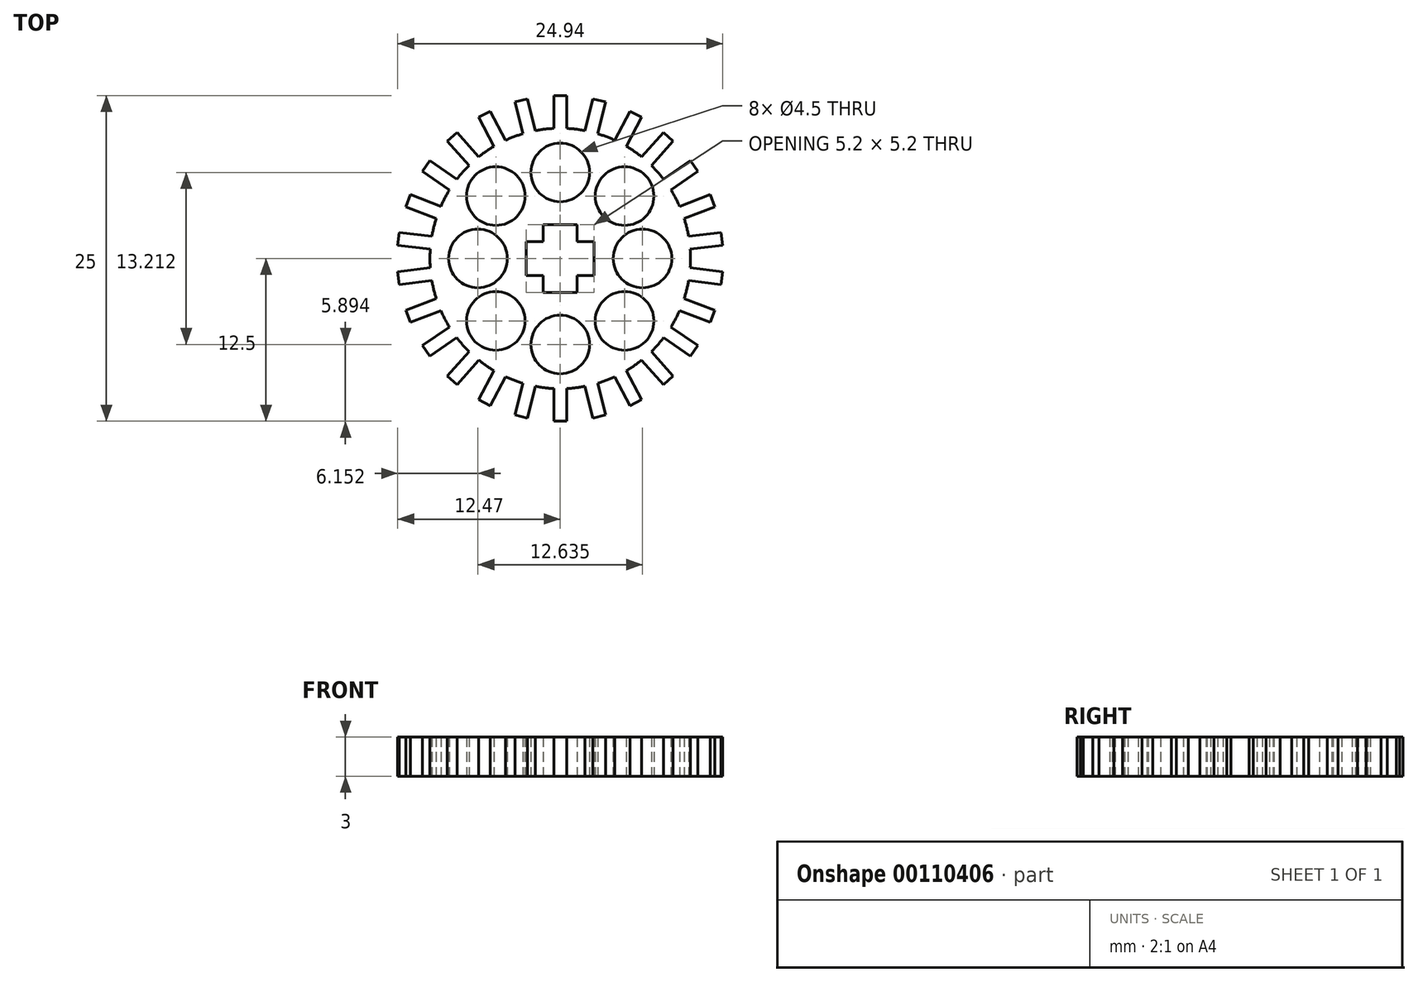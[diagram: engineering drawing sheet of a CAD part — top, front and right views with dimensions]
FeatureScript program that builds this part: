
annotation { "Feature Type Name" : "Feature", "Feature Type Description" : "" }
export const myFeature = defineFeature(function(context is Context, id is Id, definition is map)
    precondition{}
    {
        {
            var Q0;
            Q0=qCreatedBy(makeId("Top.planeOp"),FACE);
            var sketch = newSketch(context, id + "F0", { "sketchPlane" : qUnion([Q0])});
            skCircle(sketch, "E0", {"center": v(0, 0) * mm, "radius": 10 * mm});
            skLineSegment(sketch, "E1", {"start": v(0, 2.6) * mm, "end": v(1.3, 2.6) * mm});
            skLineSegment(sketch, "E2", {"start": v(1.3, 2.6) * mm, "end": v(1.3, 1.3) * mm});
            skLineSegment(sketch, "E3", {"start": v(1.3, 1.3) * mm, "end": v(2.6, 1.3) * mm});
            skLineSegment(sketch, "E4", {"start": v(2.6, 1.3) * mm, "end": v(2.6, 0) * mm});
            skLineSegment(sketch, "E5", {"start": v(2.6, 0) * mm, "end": v(2.6, -1.3) * mm});
            skLineSegment(sketch, "E6", {"start": v(2.6, -1.3) * mm, "end": v(1.3, -1.3) * mm});
            skLineSegment(sketch, "E7", {"start": v(1.3, -1.3) * mm, "end": v(1.3, -2.6) * mm});
            skLineSegment(sketch, "E8", {"start": v(1.3, -2.6) * mm, "end": v(0, -2.6) * mm});
            skLineSegment(sketch, "E9", {"start": v(0, -2.6) * mm, "end": v(-1.3, -2.6) * mm});
            skLineSegment(sketch, "E10", {"start": v(-1.3, -2.6) * mm, "end": v(-1.3, -1.3) * mm});
            skLineSegment(sketch, "E11", {"start": v(-1.3, -1.3) * mm, "end": v(-2.6, -1.3) * mm});
            skLineSegment(sketch, "E12", {"start": v(-2.6, -1.3) * mm, "end": v(-2.6, 0) * mm});
            skLineSegment(sketch, "E13", {"start": v(-2.6, 0) * mm, "end": v(-2.6, 1.3) * mm});
            skLineSegment(sketch, "E14", {"start": v(-2.6, 1.3) * mm, "end": v(-1.3, 1.3) * mm});
            skLineSegment(sketch, "E15", {"start": v(-1.3, 1.3) * mm, "end": v(-1.3, 2.6) * mm});
            skLineSegment(sketch, "E16", {"start": v(-1.3, 2.6) * mm, "end": v(0, 2.6) * mm});
            skPoint(sketch, "E17.startSnap0", {"position": v(0, 1.3) * mm});
            skPoint(sketch, "E18.endSnap0", {"position": v(-0.25, -12.5) * mm});
            skLineSegment(sketch, "E19", {"start": v(0, -12.5) * mm, "end": v(0, -10) * mm});
            skPoint(sketch, "E17.start.orphan", {"position": v(0, -10) * mm});
            skLineSegment(sketch, "E20", {"start": v(0, -12.5) * mm, "end": v(0.5, -12.5) * mm});
            skPoint(sketch, "E21.start.orphan", {"position": v(-1, -12.5) * mm});
            skPoint(sketch, "E22.orphan", {"position": v(-0.5, -12.5) * mm});
            skLineSegment(sketch, "E23", {"start": v(0, -12.5) * mm, "end": v(-0.5, -12.5) * mm});
            skLineSegment(sketch, "E24", {"start": v(-0.5, -12.5) * mm, "end": v(-0.5, -9.99) * mm});
            skLineSegment(sketch, "E25", {"start": v(0.5, -12.5) * mm, "end": v(0.5, -9.99) * mm});
            skLineSegment(sketch, "E26.1.0", {"start": v(2.5, -12.26) * mm, "end": v(1.9, -9.82) * mm});
            skLineSegment(sketch, "E26.1.1", {"start": v(3.48, -12.02) * mm, "end": v(2.88, -9.58) * mm});
            skLineSegment(sketch, "E26.1.2", {"start": v(3, -12.14) * mm, "end": v(3.48, -12.02) * mm});
            skLineSegment(sketch, "E26.1.3", {"start": v(3, -12.14) * mm, "end": v(2.5, -12.26) * mm});
            skLineSegment(sketch, "E26.2.0", {"start": v(5.37, -11.3) * mm, "end": v(4.2, -9.08) * mm});
            skLineSegment(sketch, "E26.2.1", {"start": v(6.25, -10.84) * mm, "end": v(5.08, -8.61) * mm});
            skLineSegment(sketch, "E26.2.2", {"start": v(5.8, -11.07) * mm, "end": v(6.25, -10.84) * mm});
            skLineSegment(sketch, "E26.2.3", {"start": v(5.8, -11.07) * mm, "end": v(5.37, -11.3) * mm});
            skLineSegment(sketch, "E27.1.3.0", {"start": v(7.91, -9.69) * mm, "end": v(6.25, -7.8) * mm});
            skLineSegment(sketch, "E27.3.3.0", {"start": v(8.66, -9.02) * mm, "end": v(7, -7.14) * mm});
            skLineSegment(sketch, "E27.6.3.0", {"start": v(8.29, -9.36) * mm, "end": v(8.66, -9.02) * mm});
            skLineSegment(sketch, "E27.9.3.0", {"start": v(8.29, -9.36) * mm, "end": v(7.91, -9.69) * mm});
            skLineSegment(sketch, "E27.1.4.0", {"start": v(10, -7.51) * mm, "end": v(7.94, -6.09) * mm});
            skLineSegment(sketch, "E27.3.4.0", {"start": v(10.57, -6.69) * mm, "end": v(8.5, -5.26) * mm});
            skLineSegment(sketch, "E27.6.4.0", {"start": v(10.29, -7.1) * mm, "end": v(10.57, -6.69) * mm});
            skLineSegment(sketch, "E27.9.4.0", {"start": v(10.29, -7.1) * mm, "end": v(10, -7.51) * mm});
            skLineSegment(sketch, "E27.1.5.0", {"start": v(11.51, -4.9) * mm, "end": v(9.16, -4) * mm});
            skLineSegment(sketch, "E27.3.5.0", {"start": v(11.87, -3.97) * mm, "end": v(9.52, -3.07) * mm});
            skLineSegment(sketch, "E27.6.5.0", {"start": v(11.69, -4.43) * mm, "end": v(11.87, -3.97) * mm});
            skLineSegment(sketch, "E27.9.5.0", {"start": v(11.69, -4.43) * mm, "end": v(11.51, -4.9) * mm});
            skLineSegment(sketch, "E27.1.6.0", {"start": v(12.35, -2) * mm, "end": v(9.85, -1.7) * mm});
            skLineSegment(sketch, "E27.3.6.0", {"start": v(12.47, -1.01) * mm, "end": v(9.97, -0.7) * mm});
            skLineSegment(sketch, "E27.6.6.0", {"start": v(12.4, -1.5) * mm, "end": v(12.47, -1.01) * mm});
            skLineSegment(sketch, "E27.9.6.0", {"start": v(12.4, -1.5) * mm, "end": v(12.35, -2) * mm});
            skLineSegment(sketch, "E27.1.7.0", {"start": v(12.47, 1.01) * mm, "end": v(9.97, 0.7) * mm});
            skLineSegment(sketch, "E27.3.7.0", {"start": v(12.35, 2) * mm, "end": v(9.85, 1.7) * mm});
            skLineSegment(sketch, "E27.6.7.0", {"start": v(12.4, 1.5) * mm, "end": v(12.35, 2) * mm});
            skLineSegment(sketch, "E27.9.7.0", {"start": v(12.4, 1.5) * mm, "end": v(12.47, 1.01) * mm});
            skLineSegment(sketch, "E27.1.8.0", {"start": v(11.87, 3.97) * mm, "end": v(9.52, 3.07) * mm});
            skLineSegment(sketch, "E27.3.8.0", {"start": v(11.51, 4.9) * mm, "end": v(9.16, 4) * mm});
            skLineSegment(sketch, "E27.6.8.0", {"start": v(11.69, 4.43) * mm, "end": v(11.51, 4.9) * mm});
            skLineSegment(sketch, "E27.9.8.0", {"start": v(11.69, 4.43) * mm, "end": v(11.87, 3.97) * mm});
            skLineSegment(sketch, "E27.1.9.0", {"start": v(10.57, 6.69) * mm, "end": v(8.5, 5.26) * mm});
            skLineSegment(sketch, "E27.3.9.0", {"start": v(10, 7.51) * mm, "end": v(7.94, 6.09) * mm});
            skLineSegment(sketch, "E27.6.9.0", {"start": v(10.29, 7.1) * mm, "end": v(10, 7.51) * mm});
            skLineSegment(sketch, "E27.9.9.0", {"start": v(10.29, 7.1) * mm, "end": v(10.57, 6.69) * mm});
            skLineSegment(sketch, "E27.1.10.0", {"start": v(8.66, 9.02) * mm, "end": v(7, 7.14) * mm});
            skLineSegment(sketch, "E27.3.10.0", {"start": v(7.91, 9.69) * mm, "end": v(6.25, 7.8) * mm});
            skLineSegment(sketch, "E27.6.10.0", {"start": v(8.29, 9.36) * mm, "end": v(7.91, 9.69) * mm});
            skLineSegment(sketch, "E27.9.10.0", {"start": v(8.29, 9.36) * mm, "end": v(8.66, 9.02) * mm});
            skLineSegment(sketch, "E27.1.11.0", {"start": v(6.25, 10.84) * mm, "end": v(5.08, 8.61) * mm});
            skLineSegment(sketch, "E27.3.11.0", {"start": v(5.37, 11.3) * mm, "end": v(4.2, 9.08) * mm});
            skLineSegment(sketch, "E27.6.11.0", {"start": v(5.8, 11.07) * mm, "end": v(5.37, 11.3) * mm});
            skLineSegment(sketch, "E27.9.11.0", {"start": v(5.8, 11.07) * mm, "end": v(6.25, 10.84) * mm});
            skLineSegment(sketch, "E27.1.12.0", {"start": v(3.48, 12.02) * mm, "end": v(2.88, 9.58) * mm});
            skLineSegment(sketch, "E27.3.12.0", {"start": v(2.5, 12.26) * mm, "end": v(1.9, 9.82) * mm});
            skLineSegment(sketch, "E27.6.12.0", {"start": v(3, 12.14) * mm, "end": v(2.5, 12.26) * mm});
            skLineSegment(sketch, "E27.9.12.0", {"start": v(3, 12.14) * mm, "end": v(3.48, 12.02) * mm});
            skLineSegment(sketch, "E27.1.13.0", {"start": v(0.5, 12.5) * mm, "end": v(0.5, 9.99) * mm});
            skLineSegment(sketch, "E27.3.13.0", {"start": v(-0.5, 12.5) * mm, "end": v(-0.5, 9.99) * mm});
            skLineSegment(sketch, "E27.6.13.0", {"start": v(0, 12.5) * mm, "end": v(-0.5, 12.5) * mm});
            skLineSegment(sketch, "E27.9.13.0", {"start": v(0, 12.5) * mm, "end": v(0.5, 12.5) * mm});
            skLineSegment(sketch, "E27.1.14.0", {"start": v(-2.5, 12.26) * mm, "end": v(-1.9, 9.82) * mm});
            skLineSegment(sketch, "E27.3.14.0", {"start": v(-3.48, 12.02) * mm, "end": v(-2.88, 9.58) * mm});
            skLineSegment(sketch, "E27.6.14.0", {"start": v(-3, 12.14) * mm, "end": v(-3.48, 12.02) * mm});
            skLineSegment(sketch, "E27.9.14.0", {"start": v(-3, 12.14) * mm, "end": v(-2.5, 12.26) * mm});
            skLineSegment(sketch, "E27.1.15.0", {"start": v(-5.37, 11.3) * mm, "end": v(-4.2, 9.08) * mm});
            skLineSegment(sketch, "E27.3.15.0", {"start": v(-6.25, 10.84) * mm, "end": v(-5.08, 8.61) * mm});
            skLineSegment(sketch, "E27.6.15.0", {"start": v(-5.8, 11.07) * mm, "end": v(-6.25, 10.84) * mm});
            skLineSegment(sketch, "E27.9.15.0", {"start": v(-5.8, 11.07) * mm, "end": v(-5.37, 11.3) * mm});
            skLineSegment(sketch, "E27.1.16.0", {"start": v(-7.91, 9.69) * mm, "end": v(-6.25, 7.8) * mm});
            skLineSegment(sketch, "E27.3.16.0", {"start": v(-8.66, 9.02) * mm, "end": v(-7, 7.14) * mm});
            skLineSegment(sketch, "E27.6.16.0", {"start": v(-8.29, 9.36) * mm, "end": v(-8.66, 9.02) * mm});
            skLineSegment(sketch, "E27.9.16.0", {"start": v(-8.29, 9.36) * mm, "end": v(-7.91, 9.69) * mm});
            skLineSegment(sketch, "E27.1.17.0", {"start": v(-10, 7.51) * mm, "end": v(-7.94, 6.09) * mm});
            skLineSegment(sketch, "E27.3.17.0", {"start": v(-10.57, 6.69) * mm, "end": v(-8.5, 5.26) * mm});
            skLineSegment(sketch, "E27.6.17.0", {"start": v(-10.29, 7.1) * mm, "end": v(-10.57, 6.69) * mm});
            skLineSegment(sketch, "E27.9.17.0", {"start": v(-10.29, 7.1) * mm, "end": v(-10, 7.51) * mm});
            skLineSegment(sketch, "E28.1.18.0", {"start": v(-11.51, 4.9) * mm, "end": v(-9.16, 4) * mm});
            skLineSegment(sketch, "E28.3.18.0", {"start": v(-11.87, 3.97) * mm, "end": v(-9.52, 3.07) * mm});
            skLineSegment(sketch, "E28.6.18.0", {"start": v(-11.69, 4.43) * mm, "end": v(-11.87, 3.97) * mm});
            skLineSegment(sketch, "E28.9.18.0", {"start": v(-11.69, 4.43) * mm, "end": v(-11.51, 4.9) * mm});
            skLineSegment(sketch, "E28.1.19.0", {"start": v(-12.35, 2) * mm, "end": v(-9.85, 1.7) * mm});
            skLineSegment(sketch, "E28.3.19.0", {"start": v(-12.47, 1.01) * mm, "end": v(-9.97, 0.7) * mm});
            skLineSegment(sketch, "E28.6.19.0", {"start": v(-12.4, 1.5) * mm, "end": v(-12.47, 1.01) * mm});
            skLineSegment(sketch, "E28.9.19.0", {"start": v(-12.4, 1.5) * mm, "end": v(-12.35, 2) * mm});
            skLineSegment(sketch, "E28.1.20.0", {"start": v(-12.47, -1.01) * mm, "end": v(-9.97, -0.7) * mm});
            skLineSegment(sketch, "E28.3.20.0", {"start": v(-12.35, -2) * mm, "end": v(-9.85, -1.7) * mm});
            skLineSegment(sketch, "E28.6.20.0", {"start": v(-12.4, -1.5) * mm, "end": v(-12.35, -2) * mm});
            skLineSegment(sketch, "E28.9.20.0", {"start": v(-12.4, -1.5) * mm, "end": v(-12.47, -1.01) * mm});
            skLineSegment(sketch, "E28.1.21.0", {"start": v(-11.87, -3.97) * mm, "end": v(-9.52, -3.07) * mm});
            skLineSegment(sketch, "E28.3.21.0", {"start": v(-11.51, -4.9) * mm, "end": v(-9.16, -4) * mm});
            skLineSegment(sketch, "E28.6.21.0", {"start": v(-11.69, -4.43) * mm, "end": v(-11.51, -4.9) * mm});
            skLineSegment(sketch, "E28.9.21.0", {"start": v(-11.69, -4.43) * mm, "end": v(-11.87, -3.97) * mm});
            skLineSegment(sketch, "E28.1.22.0", {"start": v(-10.57, -6.69) * mm, "end": v(-8.5, -5.26) * mm});
            skLineSegment(sketch, "E28.3.22.0", {"start": v(-10, -7.51) * mm, "end": v(-7.94, -6.09) * mm});
            skLineSegment(sketch, "E28.6.22.0", {"start": v(-10.29, -7.1) * mm, "end": v(-10, -7.51) * mm});
            skLineSegment(sketch, "E28.9.22.0", {"start": v(-10.29, -7.1) * mm, "end": v(-10.57, -6.69) * mm});
            skLineSegment(sketch, "E28.1.23.0", {"start": v(-8.66, -9.02) * mm, "end": v(-7, -7.14) * mm});
            skLineSegment(sketch, "E28.3.23.0", {"start": v(-7.91, -9.69) * mm, "end": v(-6.25, -7.8) * mm});
            skLineSegment(sketch, "E28.6.23.0", {"start": v(-8.29, -9.36) * mm, "end": v(-7.91, -9.69) * mm});
            skLineSegment(sketch, "E28.9.23.0", {"start": v(-8.29, -9.36) * mm, "end": v(-8.66, -9.02) * mm});
            skLineSegment(sketch, "E28.1.24.0", {"start": v(-6.25, -10.84) * mm, "end": v(-5.08, -8.61) * mm});
            skLineSegment(sketch, "E28.3.24.0", {"start": v(-5.37, -11.3) * mm, "end": v(-4.2, -9.08) * mm});
            skLineSegment(sketch, "E28.6.24.0", {"start": v(-5.8, -11.07) * mm, "end": v(-5.37, -11.3) * mm});
            skLineSegment(sketch, "E28.9.24.0", {"start": v(-5.8, -11.07) * mm, "end": v(-6.25, -10.84) * mm});
            skLineSegment(sketch, "E28.1.25.0", {"start": v(-3.48, -12.02) * mm, "end": v(-2.88, -9.58) * mm});
            skLineSegment(sketch, "E28.3.25.0", {"start": v(-2.5, -12.26) * mm, "end": v(-1.9, -9.82) * mm});
            skLineSegment(sketch, "E28.6.25.0", {"start": v(-3, -12.14) * mm, "end": v(-2.5, -12.26) * mm});
            skLineSegment(sketch, "E28.9.25.0", {"start": v(-3, -12.14) * mm, "end": v(-3.48, -12.02) * mm});
            skCircle(sketch, "E29", {"center": v(-4.94, 4.8) * mm, "radius": 2.25 * mm});
            skCircle(sketch, "E30.MirrorC", {"center": v(4.94, 4.8) * mm, "radius": 2.25 * mm});
            skCircle(sketch, "E31.MirrorC", {"center": v(4.94, -4.8) * mm, "radius": 2.25 * mm});
            skCircle(sketch, "E32.MirrorC", {"center": v(-4.94, -4.8) * mm, "radius": 2.25 * mm});
            skCircle(sketch, "E33", {"center": v(0, 6.6) * mm, "radius": 2.25 * mm});
            skCircle(sketch, "E34.MirrorC", {"center": v(0, -6.6) * mm, "radius": 2.25 * mm});
            skCircle(sketch, "E35", {"center": v(6.32, 0) * mm, "radius": 2.25 * mm});
            skCircle(sketch, "E36.MirrorC", {"center": v(-6.32, 0) * mm, "radius": 2.25 * mm});
            skSolve(sketch);
        }
        {
            var Q0;
            Q0 = qSketchRegion(id + "F0", true);
            extrude(context, id + "F1", {"entities" : qUnion([Q0]), "depth" : 3 * mm});
        }
    });
